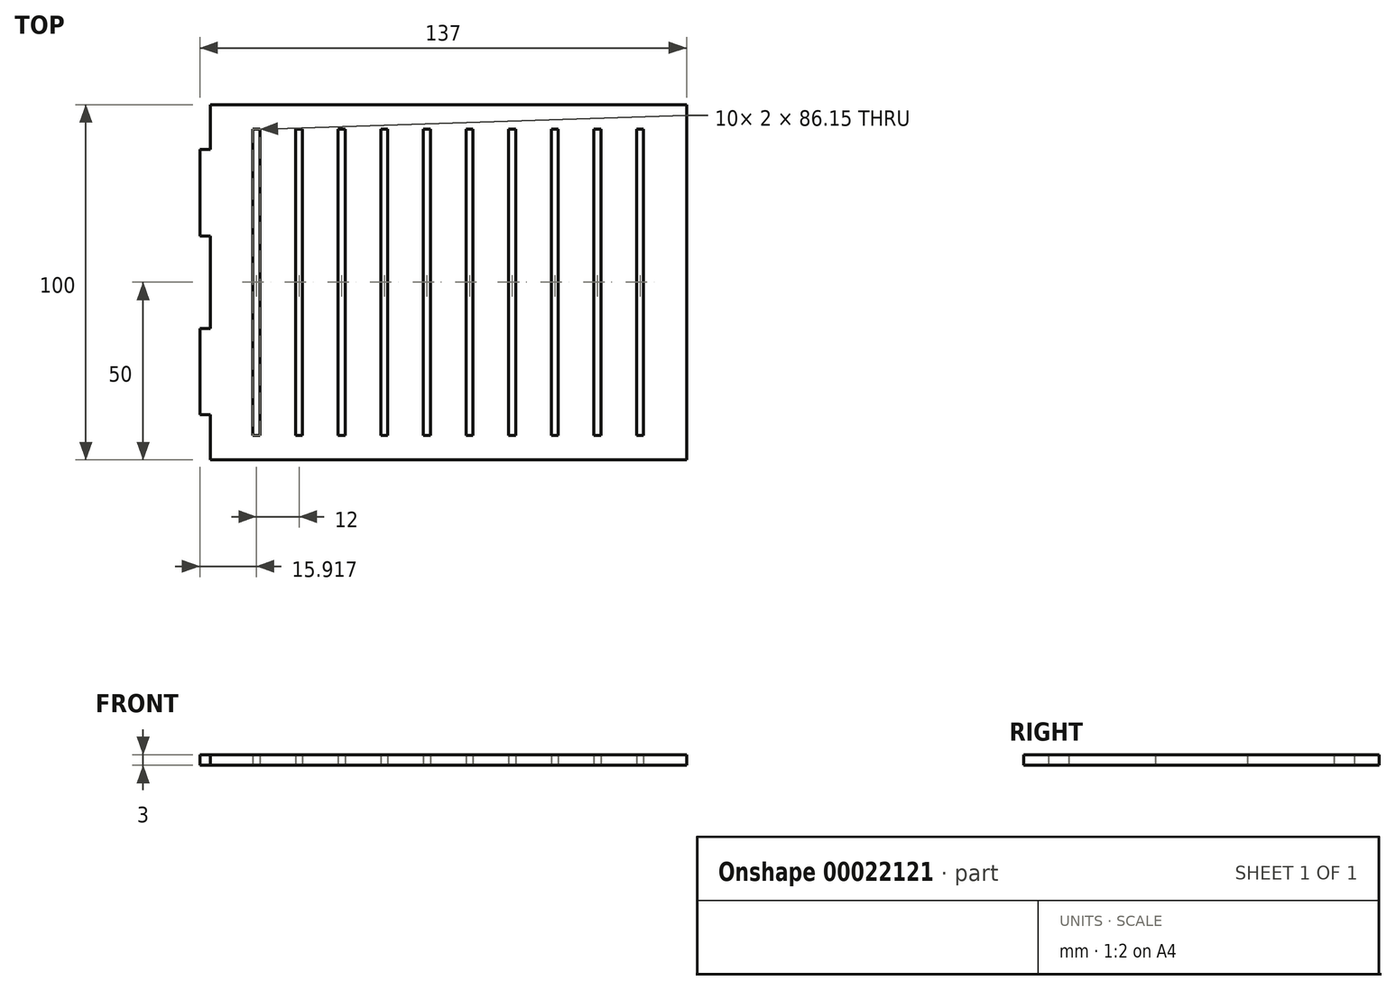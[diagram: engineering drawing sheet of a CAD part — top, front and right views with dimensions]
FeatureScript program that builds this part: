
annotation { "Feature Type Name" : "Feature", "Feature Type Description" : "" }
export const myFeature = defineFeature(function(context is Context, id is Id, definition is map)
    precondition{}
    {
        {
            var Q0;
            Q0=qCreatedBy(makeId("Top.planeOp"),FACE);
            var sketch = newSketch(context, id + "F0", { "sketchPlane" : qUnion([Q0])});
            skLineSegment(sketch, "E0.rect.bottom", {"start": v(67, -50) * mm, "end": v(-67, -50) * mm});
            skLineSegment(sketch, "E0.rect.top", {"start": v(67, 50) * mm, "end": v(-67, 50) * mm});
            skLineSegment(sketch, "E0.rect.left", {"start": v(67, -50) * mm, "end": v(67, 50) * mm});
            skLineSegment(sketch, "E0.rect.right", {"start": v(-67, -50) * mm, "end": v(-67, -37.34) * mm});
            skPoint(sketch, "E0.rect.middle", {"position": v(0, 0) * mm});
            skLineSegment(sketch, "E1.bottom", {"start": v(-67, 37.34) * mm, "end": v(-70, 37.34) * mm});
            skLineSegment(sketch, "E1.top", {"start": v(-67, 13) * mm, "end": v(-70, 13) * mm});
            skLineSegment(sketch, "E1.right", {"start": v(-70, 37.34) * mm, "end": v(-70, 13) * mm});
            skLineSegment(sketch, "E2.MirrorCS", {"start": v(-70, -37.34) * mm, "end": v(-70, -13) * mm});
            skLineSegment(sketch, "E3.MirrorCS", {"start": v(-67, -37.34) * mm, "end": v(-70, -37.34) * mm});
            skLineSegment(sketch, "E4.MirrorCS", {"start": v(-67, -13) * mm, "end": v(-70, -13) * mm});
            skLineSegment(sketch, "E5.trimOffspring", {"start": v(-67, -13) * mm, "end": v(-67, 13) * mm});
            skLineSegment(sketch, "E6.trimOffspring", {"start": v(-67, 37.34) * mm, "end": v(-67, 50) * mm});
            skLineSegment(sketch, "E7.rect.bottom", {"start": v(-53.08, -43.08) * mm, "end": v(-55.08, -43.08) * mm});
            skLineSegment(sketch, "E7.rect.top", {"start": v(-53.08, 43.08) * mm, "end": v(-55.08, 43.08) * mm});
            skLineSegment(sketch, "E7.rect.left", {"start": v(-53.08, -43.08) * mm, "end": v(-53.08, 43.08) * mm});
            skLineSegment(sketch, "E7.rect.right", {"start": v(-55.08, -43.08) * mm, "end": v(-55.08, 43.08) * mm});
            skLineSegment(sketch, "E8.1.0.0", {"start": v(-43.08, -43.08) * mm, "end": v(-43.08, 43.08) * mm});
            skLineSegment(sketch, "E8.1.0.1", {"start": v(-41.08, -43.08) * mm, "end": v(-41.08, 43.08) * mm});
            skLineSegment(sketch, "E8.1.0.2", {"start": v(-41.08, -43.08) * mm, "end": v(-43.08, -43.08) * mm});
            skLineSegment(sketch, "E8.1.0.3", {"start": v(-41.08, 43.08) * mm, "end": v(-43.08, 43.08) * mm});
            skLineSegment(sketch, "E8.2.0.0", {"start": v(-31.08, -43.08) * mm, "end": v(-31.08, 43.08) * mm});
            skLineSegment(sketch, "E8.2.0.1", {"start": v(-29.08, -43.08) * mm, "end": v(-29.08, 43.08) * mm});
            skLineSegment(sketch, "E8.2.0.2", {"start": v(-29.08, -43.08) * mm, "end": v(-31.08, -43.08) * mm});
            skLineSegment(sketch, "E8.2.0.3", {"start": v(-29.08, 43.08) * mm, "end": v(-31.08, 43.08) * mm});
            skLineSegment(sketch, "E8.3.0.0", {"start": v(-19.08, -43.08) * mm, "end": v(-19.08, 43.08) * mm});
            skLineSegment(sketch, "E8.3.0.1", {"start": v(-17.08, -43.08) * mm, "end": v(-17.08, 43.08) * mm});
            skLineSegment(sketch, "E8.3.0.2", {"start": v(-17.08, -43.08) * mm, "end": v(-19.08, -43.08) * mm});
            skLineSegment(sketch, "E8.3.0.3", {"start": v(-17.08, 43.08) * mm, "end": v(-19.08, 43.08) * mm});
            skLineSegment(sketch, "E8.4.0.0", {"start": v(-7.08, -43.08) * mm, "end": v(-7.08, 43.08) * mm});
            skLineSegment(sketch, "E8.4.0.1", {"start": v(-5.08, -43.08) * mm, "end": v(-5.08, 43.08) * mm});
            skLineSegment(sketch, "E8.4.0.2", {"start": v(-5.08, -43.08) * mm, "end": v(-7.08, -43.08) * mm});
            skLineSegment(sketch, "E8.4.0.3", {"start": v(-5.08, 43.08) * mm, "end": v(-7.08, 43.08) * mm});
            skLineSegment(sketch, "E8.5.0.0", {"start": v(4.92, -43.08) * mm, "end": v(4.92, 43.08) * mm});
            skLineSegment(sketch, "E8.5.0.1", {"start": v(6.92, -43.08) * mm, "end": v(6.92, 43.08) * mm});
            skLineSegment(sketch, "E8.5.0.2", {"start": v(6.92, -43.08) * mm, "end": v(4.92, -43.08) * mm});
            skLineSegment(sketch, "E8.5.0.3", {"start": v(6.92, 43.08) * mm, "end": v(4.92, 43.08) * mm});
            skLineSegment(sketch, "E8.6.0.0", {"start": v(16.92, -43.08) * mm, "end": v(16.92, 43.08) * mm});
            skLineSegment(sketch, "E8.6.0.1", {"start": v(18.92, -43.08) * mm, "end": v(18.92, 43.08) * mm});
            skLineSegment(sketch, "E8.6.0.2", {"start": v(18.92, -43.08) * mm, "end": v(16.92, -43.08) * mm});
            skLineSegment(sketch, "E8.6.0.3", {"start": v(18.92, 43.08) * mm, "end": v(16.92, 43.08) * mm});
            skLineSegment(sketch, "E8.7.0.0", {"start": v(28.92, -43.08) * mm, "end": v(28.92, 43.08) * mm});
            skLineSegment(sketch, "E8.7.0.1", {"start": v(30.92, -43.08) * mm, "end": v(30.92, 43.08) * mm});
            skLineSegment(sketch, "E8.7.0.2", {"start": v(30.92, -43.08) * mm, "end": v(28.92, -43.08) * mm});
            skLineSegment(sketch, "E8.7.0.3", {"start": v(30.92, 43.08) * mm, "end": v(28.92, 43.08) * mm});
            skLineSegment(sketch, "E8.8.0.0", {"start": v(40.92, -43.08) * mm, "end": v(40.92, 43.08) * mm});
            skLineSegment(sketch, "E8.8.0.1", {"start": v(42.92, -43.08) * mm, "end": v(42.92, 43.08) * mm});
            skLineSegment(sketch, "E8.8.0.2", {"start": v(42.92, -43.08) * mm, "end": v(40.92, -43.08) * mm});
            skLineSegment(sketch, "E8.8.0.3", {"start": v(42.92, 43.08) * mm, "end": v(40.92, 43.08) * mm});
            skLineSegment(sketch, "E8.9.0.0", {"start": v(52.92, -43.08) * mm, "end": v(52.92, 43.08) * mm});
            skLineSegment(sketch, "E8.9.0.1", {"start": v(54.92, -43.08) * mm, "end": v(54.92, 43.08) * mm});
            skLineSegment(sketch, "E8.9.0.2", {"start": v(54.92, -43.08) * mm, "end": v(52.92, -43.08) * mm});
            skLineSegment(sketch, "E8.9.0.3", {"start": v(54.92, 43.08) * mm, "end": v(52.92, 43.08) * mm});
            skLineSegment(sketch, "E8.direction1", {"start": v(-55.08, -43.08) * mm, "end": v(-43.08, -43.08) * mm, "construction": true});
            skSolve(sketch);
        }
        {
            var Q0;
            Q0 = qSketchRegion(id + "F0", true);
            extrude(context, id + "F1", {"entities" : qUnion([Q0]), "depth" : 3 * mm});
        }
    });
